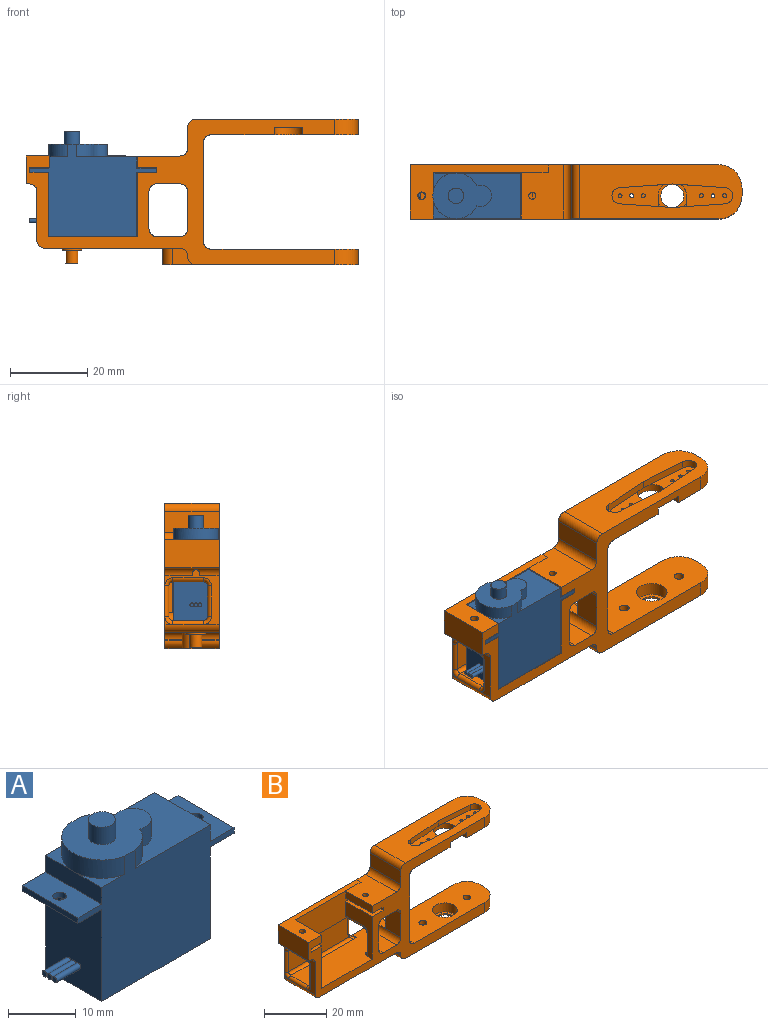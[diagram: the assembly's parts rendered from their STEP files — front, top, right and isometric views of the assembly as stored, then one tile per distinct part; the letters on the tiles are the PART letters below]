
ASSEMBLY  parts=2 mates=1
PART A: 31 faces, bbox 32.7x11.7x27.1 mm
  f0: plane 15.71x11.7mm, normal (0,0,1), area 125.7mm2, adj f3,f4,f6,f19,f20,f21
  f1: plane 5.85x4.86mm, normal (0,0,1), area 7.1mm2, adj f2,f4,f18
  f2: plane 11.7x3mm, normal (-1,0,0), area 35.1mm2, adj f1,f4,f6,f9,f17
  f3: plane 11.7x3mm, normal (1,0,0), area 35.1mm2, adj f0,f4,f6,f13
  f4: plane 32.6x23.9mm, normal (0,1,0), area 485.7mm2, adj f0,f1,f2,f3,f5,f7,f8,f10
  f5: plane 16.6x11.7mm, normal (-1,0,0), area 191.9mm2, adj f4,f6,f8,f16,f25,f27,f29
  f6: plane 32.6x23.9mm, normal (0,-1,0), area 485.7mm2, adj f0,f2,f3,f5,f7,f8,f9,f10
  f7: plane 16.6x11.7mm, normal (1,0,0), area 194.2mm2, adj f4,f6,f8,f12
  f8: plane 22.75x11.7mm, normal (0,0,-1), area 266.2mm2, adj f4,f5,f6,f7
  f9: plane 5.85x4.86mm, normal (0,0,1), area 7.1mm2, adj f2,f6,f18
  f10: plane 11.7x1mm, normal (1,0,0), area 11.7mm2, adj f4,f6,f12,f13
  f11: cylinder r=1mm len=2mm, axis (0,0,1), area 6.3mm2, adj f12,f13
  f12: plane 11.7x4.93mm, normal (0,0,-1), area 54.5mm2, adj f4,f6,f7,f10,f11
  f13: plane 11.7x4.93mm, normal (0,0,1), area 54.5mm2, adj f3,f4,f6,f10,f11
  f14: cylinder r=1mm len=2mm, axis (0,0,1), area 6.3mm2, adj f16,f17
  f15: plane 11.7x1mm, normal (-1,0,0), area 11.7mm2, adj f4,f6,f16,f17
  f16: plane 11.7x4.93mm, normal (0,0,-1), area 54.5mm2, adj f4,f5,f6,f14,f15
  f17: plane 11.7x4.93mm, normal (0,0,1), area 54.5mm2, adj f2,f4,f6,f14,f15
  f18: cylinder r=5.95mm len=11.7mm, axis (0,0,-1), area 54.5mm2, adj f1,f4,f6,f9,f22
  f19: cylinder r=5.95mm len=4.29mm, axis (0,0,-1), area 18.5mm2, adj f0,f6,f20,f22
  f20: cylinder r=2.75mm len=5.5mm, axis (0,0,-1), area 35.4mm2, adj f0,f19,f21,f22
  f21: cylinder r=5.95mm len=4.29mm, axis (0,0,-1), area 18.5mm2, adj f0,f4,f20,f22
  f22: plane 15.1x11.7mm, normal (0,0,1), area 113.8mm2, adj f4,f6,f18,f19,f20,f21,f23
  f23: cylinder r=2mm len=4mm, axis (0,0,-1), area 39.6mm2, adj f22,f24
  f24: plane 4x4mm, normal (0,0,1), area 12.6mm2, adj f23
  f25: cylinder r=0.5mm len=5mm, axis (1,0,0), area 15.7mm2, adj f5,f26
  f26: plane 1x1mm, normal (-1,0,0), area 0.8mm2, adj f25
  f27: cylinder r=0.5mm len=5mm, axis (1,0,0), area 15.7mm2, adj f5,f28
  f28: plane 1x1mm, normal (-1,0,0), area 0.8mm2, adj f27
  f29: cylinder r=0.5mm len=5mm, axis (1,0,0), area 15.7mm2, adj f5,f30
  f30: plane 1x1mm, normal (-1,0,0), area 0.8mm2, adj f29
PART B: 145 faces, bbox 86.1x15.3x37.9 mm
  f0: plane 2x0.1mm, normal (-1,0,0), area 0.2mm2, adj f29,f31,f32,f140
  f1: plane 34.95x14mm, normal (0,0,-1), area 449mm2, adj f3,f28,f32,f58,f84,f92,f127,f128
  f2: plane 4.5x0.25mm, normal (-1,0,0), area 1.1mm2, adj f3,f4,f32,f128
  f3: cylinder r=2mm len=4.5mm, axis (0,-1,0), area 14.1mm2, adj f1,f2,f32,f128
  f4: cylinder r=2mm len=4.5mm, axis (0,1,0), area 14.1mm2, adj f2,f32,f34,f128
  f5: plane 2x2mm, normal (-1,0,0), area 0.9mm2, adj f32,f92,f121
  f6: plane 25.5x14mm, normal (1,0,0), area 299.4mm2, adj f28,f32,f81,f86,f96,f97,f98,f132
  f7: plane 9.6x2.5mm, normal (-1,0,0), area 19.3mm2, adj f32,f89,f91,f102,f103,f104
  f8: plane 10.1x9.6mm, normal (-1,0,0), area 80.8mm2, adj f28,f89,f91,f96,f97,f98,f99,f100
  f9: cylinder r=3.96mm len=7.92mm, axis (0,0,-1), area 87.1mm2, adj f36,f95
  f10: plane 13.32x5.68mm, normal (0,0,1), area 53.7mm2, adj f62,f63,f64,f72,f73,f75,f76,f80
  f11: plane 13.32x5.68mm, normal (0,0,1), area 53.7mm2, adj f65,f66,f67,f72,f74,f77,f78,f79
  f12: plane 38x14mm, normal (0,0,-1), area 446.3mm2, adj f28,f32,f37,f68,f71,f72,f73,f74
  f13: plane 7.37x3.21mm, normal (0,0,-1), area 22.7mm2, adj f28,f64,f65,f73,f74
  f14: plane 4.57x0.79mm, normal (0,0,-1), area 2.1mm2, adj f62,f67,f72
  f15: plane 42x14mm, normal (0,0,1), area 419.6mm2, adj f28,f32,f37,f62,f63,f64,f65,f66
  f16: plane 14.6x14mm, normal (-1,0,0), area 38.6mm2, adj f28,f32,f42,f43,f83,f92,f115,f116
  f17: plane 14x11.6mm, normal (1,0,0), area 31.6mm2, adj f28,f32,f44,f45,f90,f93,f108,f109
  f18: plane 14x6mm, normal (0,0,-1), area 84mm2, adj f28,f32,f89,f93
  f19: plane 14x11mm, normal (0,0,1), area 137.6mm2, adj f20,f28,f30,f32,f46,f88
  f20: plane 12x2.9mm, normal (-1,0,0), area 34.8mm2, adj f19,f21,f28,f29
  f21: plane 12x4.93mm, normal (0,0,-1), area 56.6mm2, adj f20,f22,f28,f29,f46
  f22: plane 12x1.3mm, normal (-1,0,0), area 15.6mm2, adj f21,f23,f28,f29
  f23: plane 12x4.93mm, normal (0,0,1), area 56.6mm2, adj f22,f24,f28,f29,f44
  f24: plane 16.6x12mm, normal (-1,0,0), area 90.1mm2, adj f23,f25,f28,f29,f123,f124,f125,f126
  f25: plane 36.32x14.37mm, normal (0,0,1), area 416mm2, adj f24,f26,f28,f32,f47,f51,f57,f82
  f26: plane 16.6x12mm, normal (1,0,0), area 109.6mm2, adj f25,f27,f28,f29,f51,f52,f53,f54
  f27: plane 12x4.83mm, normal (0,0,1), area 55.4mm2, adj f26,f28,f29,f43,f142
  f28: plane 79.78x37.5mm, normal (0,-1,0), area 734.1mm2, adj f1,f6,f8,f12,f13,f15,f16,f17
  f29: plane 32.7x10.8mm, normal (0,-1,0), area 259.9mm2, adj f0,f20,f21,f22,f23,f24,f26,f27
  f30: plane 35.7x14mm, normal (0,0,1), area 139.6mm2, adj f19,f28,f29,f32,f139,f141,f144
  f31: plane 4.95x2mm, normal (0,0,1), area 9.9mm2, adj f0,f29,f32,f142
  f32: plane 79.78x37.5mm, normal (0,1,0), area 1238.1mm2, adj f0,f1,f2,f3,f4,f5,f6,f7
  f33: plane 4.5x0.25mm, normal (-1,0,0), area 1.1mm2, adj f28,f84,f85,f127
  f34: plane 50.5x14mm, normal (0,0,-1), area 565.2mm2, adj f4,f28,f32,f35,f39,f40,f41,f69
  f35: plane 4x2mm, normal (1,0,0), area 8mm2, adj f34,f36,f69,f70
  f36: plane 38x14mm, normal (0,0,1), area 455mm2, adj f9,f28,f32,f35,f39,f40,f41,f69
  f37: plane 4x2mm, normal (1,0,0), area 8mm2, adj f12,f15,f68,f71
  f38: plane 14x5.45mm, normal (-1,0,0), area 76.3mm2, adj f28,f32,f87,f88
  f39: cylinder r=1.25mm len=4mm, axis (0,0,-1), area 31.4mm2, adj f34,f36
  f40: cylinder r=1.25mm len=4mm, axis (0,0,-1), area 31.4mm2, adj f34,f36
  f41: cylinder r=1.25mm len=4mm, axis (0,0,-1), area 31.4mm2, adj f34,f36,f86
  f42: plane 1.8x1.08mm, normal (0,0,1), area 1.6mm2, adj f16,f43
  f43: cylinder r=0.9mm len=4.99mm, axis (0,0,-1), area 18.9mm2, adj f16,f27,f42,f83
  f44: cylinder r=0.9mm len=5mm, axis (0,0,-1), area 18.9mm2, adj f17,f23,f45,f93
  f45: plane 1.8x1.08mm, normal (0,0,1), area 1.6mm2, adj f17,f44
  f46: cylinder r=0.9mm len=2.9mm, axis (0,0,-1), area 16.4mm2, adj f19,f21
  f47: cylinder r=1mm len=4mm, axis (-1,0,0), area 4.1mm2, adj f25,f48,f106,f123
  f48: plane 8x1.17mm, normal (0,1,0), area 8.1mm2, adj f47,f49,f107,f108,f124
  f49: cylinder r=1mm len=1mm, axis (-1,0,0), area 1.6mm2, adj f48,f50,f109,f125
  f50: plane 8x1mm, normal (0,0,-1), area 8mm2, adj f49,f55,f110,f126
  f51: cylinder r=1mm len=2mm, axis (-1,0,0), area 3.1mm2, adj f25,f26,f52,f117
  f52: plane 8x2mm, normal (0,1,0), area 16mm2, adj f26,f51,f53,f115
  f53: cylinder r=1mm len=2mm, axis (-1,0,0), area 3.1mm2, adj f26,f52,f54,f116
  f54: plane 8x2mm, normal (0,0,-1), area 16mm2, adj f26,f53,f55,f118
  f55: cylinder r=1mm len=26.95mm, axis (-1,0,0), area 42.3mm2, adj f29,f50,f54,f56,f111,f120
  f56: plane 27.12x8mm, normal (0,-1,0), area 215.7mm2, adj f55,f57,f112,f113,f122
  f57: cylinder r=1mm len=29.95mm, axis (-1,0,0), area 44.8mm2, adj f25,f56,f114,f121
  f58: cylinder r=2.56mm len=5.11mm, axis (0,0,1), area 8mm2, adj f1,f59
  f59: plane 5.11x5.11mm, normal (0,0,-1), area 12.9mm2, adj f58,f61
  f60: plane 3.11x3.11mm, normal (0,0,-1), area 7.6mm2, adj f61
  f61: cylinder r=1.55mm len=3.5mm, axis (0,0,1), area 34.2mm2, adj f59,f60
  f62: plane 13.5x2mm, normal (0.07,-1,0), area 27.1mm2, adj f10,f14,f15,f63,f67
  f63: cylinder r=2.1mm len=4.2mm, axis (0,0,1), area 13.2mm2, adj f10,f15,f62,f64
  f64: plane 13.5x2mm, normal (0.07,1,0), area 27.1mm2, adj f10,f13,f15,f63,f65
  f65: plane 13.5x2mm, normal (-0.07,1,0), area 27.1mm2, adj f11,f13,f15,f64,f66
  f66: cylinder r=2.1mm len=4.2mm, axis (0,0,1), area 13.2mm2, adj f11,f15,f65,f67
  f67: plane 13.5x2mm, normal (-0.07,-1,0), area 27.1mm2, adj f11,f14,f15,f62,f66
  f68: cylinder r=6mm len=6mm, axis (0,0,-1), area 37.7mm2, adj f12,f15,f28,f37
  f69: cylinder r=6mm len=6mm, axis (0,0,-1), area 37.7mm2, adj f28,f34,f35,f36
  f70: cylinder r=6mm len=6mm, axis (0,0,-1), area 37.7mm2, adj f32,f34,f35,f36
  f71: cylinder r=6mm len=6mm, axis (0,0,-1), area 37.7mm2, adj f12,f15,f32,f37
  f72: cylinder r=3.68mm len=7.37mm, axis (0,0,1), area 23.1mm2, adj f10,f11,f12,f14,f73,f74
  f73: plane 6x2mm, normal (1,0,0), area 12mm2, adj f10,f12,f13,f28,f72
  f74: plane 6x2mm, normal (-1,0,0), area 12mm2, adj f11,f12,f13,f28,f72
  f75: cylinder r=0.5mm len=2mm, axis (0,0,-1), area 6.3mm2, adj f10,f12
  f76: cylinder r=0.5mm len=2mm, axis (0,0,-1), area 6.3mm2, adj f10,f12
  f77: cylinder r=0.5mm len=2mm, axis (0,0,-1), area 6.3mm2, adj f11,f12
  f78: cylinder r=0.5mm len=2mm, axis (0,0,-1), area 6.3mm2, adj f11,f12
  f79: cylinder r=0.5mm len=2mm, axis (0,0,-1), area 6.3mm2, adj f11,f12
  f80: cylinder r=0.5mm len=2mm, axis (0,0,-1), area 6.3mm2, adj f10,f12
  f81: cylinder r=2mm len=14mm, axis (0,1,0), area 44mm2, adj f6,f12,f28,f32
  f82: cylinder r=2mm len=2mm, axis (0,1,0), area 2.5mm2, adj f25,f32,f114
  f83: cylinder r=2mm len=14mm, axis (0,1,0), area 38.9mm2, adj f16,f28,f32,f43,f143
  f84: cylinder r=2mm len=4.5mm, axis (0,-1,0), area 14.1mm2, adj f1,f28,f33,f127
  f85: cylinder r=2mm len=4.5mm, axis (0,1,0), area 14.1mm2, adj f28,f33,f34,f127
  f86: cylinder r=2mm len=14mm, axis (0,-1,0), area 41.4mm2, adj f6,f28,f32,f36,f41
  f87: cylinder r=2mm len=14mm, axis (0,1,0), area 44mm2, adj f15,f28,f32,f38
  f88: cylinder r=2mm len=14mm, axis (0,-1,0), area 44mm2, adj f19,f28,f32,f38
  f89: cylinder r=2mm len=14mm, axis (0,-1,0), area 44mm2, adj f7,f8,f18,f28,f32,f105
  f90: cylinder r=2mm len=4mm, axis (0,1,0), area 8.7mm2, adj f17,f25,f28,f106,f107
  f91: cylinder r=2mm len=14mm, axis (0,1,0), area 44mm2, adj f7,f8,f25,f28,f32,f101
  f92: cylinder r=2mm len=14mm, axis (0,1,0), area 44mm2, adj f1,f5,f16,f28,f32,f119
  f93: cylinder r=2mm len=14mm, axis (0,-1,0), area 41.4mm2, adj f17,f18,f28,f32,f44
  f94: cylinder r=2.96mm len=5.92mm, axis (0,0,-1), area 9.3mm2, adj f34,f95
  f95: plane 7.92x7.92mm, normal (0,0,1), area 21.7mm2, adj f9,f94
  f96: plane 4.45x4mm, normal (0,1,0), area 14mm2, adj f6,f8,f97,f105,f132
  f97: cylinder r=1mm len=4mm, axis (-1,0,0), area 6.3mm2, adj f6,f8,f96,f98
  f98: plane 4x3.1mm, normal (0,0,-1), area 8.6mm2, adj f6,f8,f97,f99,f138
  f99: plane 4.65x3mm, normal (0,1,0), area 13.9mm2, adj f8,f98,f100,f138
  f100: cylinder r=0.5mm len=3mm, axis (-1,0,0), area 2.4mm2, adj f8,f99,f101,f137
  f101: plane 4x3mm, normal (0,0,1), area 12mm2, adj f91,f100,f102,f136
  f102: cylinder r=0.5mm len=3mm, axis (-1,0,0), area 2.4mm2, adj f7,f101,f103,f135
  f103: plane 8.6x3mm, normal (0,-1,0), area 25.8mm2, adj f7,f102,f104,f134
  f104: cylinder r=0.5mm len=3mm, axis (-1,0,0), area 2.4mm2, adj f7,f103,f105,f133
  f105: plane 3x1.4mm, normal (0,0,-1), area 4.2mm2, adj f89,f96,f104,f132
  f106: bspline ~2.94x2mm, area 1.5mm2, adj f47,f90,f107
  f107: torus R=3mm, axis (0,1,0), area 1.3mm2, adj f48,f90,f106,f108
  f108: cylinder r=1mm len=7mm, axis (0,0,-1), area 11mm2, adj f17,f48,f107,f109
  f109: torus R=2mm, axis (-1,0,0), area 3.4mm2, adj f17,f49,f108,f110
  f110: cylinder r=1mm len=8mm, axis (0,-1,0), area 12.6mm2, adj f17,f50,f109,f111
  f111: torus R=2mm, axis (-1,0,0), area 3.4mm2, adj f17,f55,f110,f112
  f112: cylinder r=1mm len=7mm, axis (0,0,1), area 11mm2, adj f32,f56,f111,f113
  f113: torus R=3mm, axis (0,1,0), area 1.3mm2, adj f32,f56,f112,f114
  f114: bspline ~2.94x2mm, area 1.5mm2, adj f57,f82,f113
  f115: cylinder r=1mm len=8mm, axis (0,0,1), area 12.6mm2, adj f16,f52,f116,f117
  f116: torus R=2mm, axis (1,0,0), area 3.4mm2, adj f16,f53,f115,f118
  f117: torus R=2mm, axis (1,0,0), area 3.4mm2, adj f16,f51,f115,f119
  f118: cylinder r=1mm len=8mm, axis (0,1,0), area 12.6mm2, adj f16,f54,f116,f120
  f119: cylinder r=1mm len=8mm, axis (0,-1,0), area 12.6mm2, adj f25,f92,f117,f121
  f120: torus R=2mm, axis (1,0,0), area 3.4mm2, adj f16,f55,f118,f122
  f121: torus R=2mm, axis (1,0,0), area 3.4mm2, adj f5,f57,f119,f122
  f122: cylinder r=1mm len=8mm, axis (0,0,-1), area 12.6mm2, adj f32,f56,f120,f121
  f123: torus R=2mm, axis (-1,0,0), area 2.1mm2, adj f24,f25,f47,f124
  f124: cylinder r=1mm len=8mm, axis (0,0,-1), area 12.6mm2, adj f24,f48,f123,f125
  f125: torus R=2mm, axis (-1,0,0), area 3.4mm2, adj f24,f49,f124,f126
  f126: cylinder r=1mm len=8mm, axis (0,-1,0), area 12.6mm2, adj f24,f29,f50,f125
  f127: plane 6x4.25mm, normal (0,-1,0), area 17mm2, adj f1,f33,f34,f84,f85,f129
  f128: plane 6x4.25mm, normal (0,1,0), area 17mm2, adj f1,f2,f3,f4,f34,f129
  f129: cylinder r=2.5mm len=5mm, axis (0,0,-1), area 33.4mm2, adj f1,f34,f127,f128
  f130: cylinder r=1.25mm len=4.25mm, axis (0,0,-1), area 33.4mm2, adj f34,f131
  f131: plane 2.5x2.5mm, normal (0,0,-1), area 4.9mm2, adj f130
  f132: cylinder r=1mm len=1.4mm, axis (0,-1,0), area 2.2mm2, adj f6,f96,f105,f133
  f133: torus R=1.5mm, axis (-1,0,0), area 2.1mm2, adj f6,f104,f132,f134
  f134: cylinder r=1mm len=8.6mm, axis (0,0,1), area 13.5mm2, adj f6,f103,f133,f135
  f135: torus R=1.5mm, axis (-1,0,0), area 2.1mm2, adj f6,f102,f134,f136
  f136: cylinder r=1mm len=4mm, axis (0,1,0), area 6.3mm2, adj f6,f101,f135,f137
  f137: torus R=1.5mm, axis (-1,0,0), area 2.1mm2, adj f6,f100,f136,f138
  f138: cylinder r=1mm len=4.65mm, axis (0,0,-1), area 7.3mm2, adj f6,f98,f99,f137
  f139: plane 12x2.9mm, normal (1,0,0), area 34.8mm2, adj f28,f29,f30,f140
  f140: plane 14x4.95mm, normal (0,0,-1), area 66.1mm2, adj f0,f28,f32,f139,f141,f142
  f141: cylinder r=1mm len=2.9mm, axis (0,0,1), area 18.2mm2, adj f30,f140
  f142: plane 14x1.3mm, normal (1,0,0), area 15.8mm2, adj f27,f28,f29,f31,f32,f140
  f143: plane 14x1mm, normal (0,0,-1), area 14mm2, adj f28,f32,f83,f144
  f144: plane 14x7.2mm, normal (-1,0,0), area 100.8mm2, adj f28,f30,f32,f143
PLACE A t=(16.09,7.36,2.23)mm fixed
PLACE B t=(16.09,7.36,2.43)mm
MATE fastened A.f14 <-> B.f43  axis (0,0,-1) through (1.79,7.36,1.23)mm
